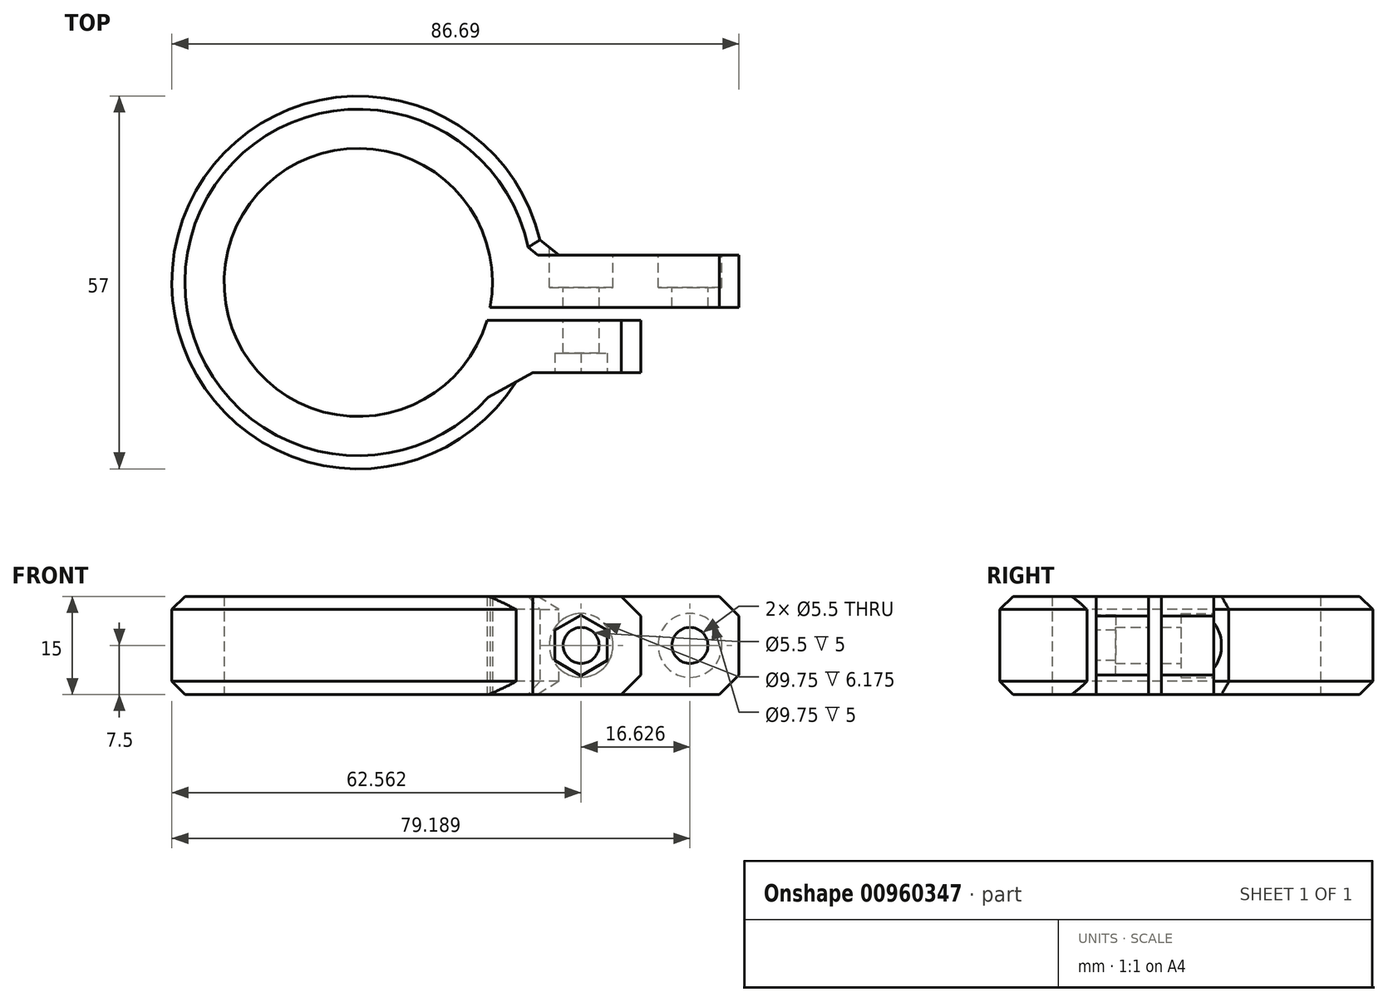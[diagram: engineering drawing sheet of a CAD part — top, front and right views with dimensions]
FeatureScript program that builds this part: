
annotation { "Feature Type Name" : "Feature", "Feature Type Description" : "" }
export const myFeature = defineFeature(function(context is Context, id is Id, definition is map)
    precondition{}
    {
        {
            var Q0;
            Q0=qCreatedBy(makeId("Top.planeOp"),FACE);
            var sketch = newSketch(context, id + "F0", { "sketchPlane" : qUnion([Q0])});
            skArc(sketch, "E0", {"start": v(20.14, -3.8) * mm, "mid": v(-19.93, 4.8) * mm, "end": v(19.66, -5.8) * mm});
            skLineSegment(sketch, "E1.bottom", {"start": v(43.19, -13.8) * mm, "end": v(24.94, -13.8) * mm});
            skLineSegment(sketch, "E1.top", {"start": v(43.19, 4.2) * mm, "end": v(28.19, 4.2) * mm});
            skLineSegment(sketch, "E1.left", {"start": v(43.19, -13.8) * mm, "end": v(43.19, -5.8) * mm});
            skLineSegment(sketch, "E2.bottom", {"start": v(43.19, -5.8) * mm, "end": v(19.66, -5.8) * mm});
            skLineSegment(sketch, "E2.top", {"start": v(43.19, -3.8) * mm, "end": v(20.14, -3.8) * mm});
            skLineSegment(sketch, "E3.trimOffspring", {"start": v(43.19, -3.8) * mm, "end": v(43.19, 4.2) * mm});
            skArc(sketch, "E4.trimOffspring", {"start": v(28.19, 4.2) * mm, "mid": v(-28.05, 5.07) * mm, "end": v(24.94, -13.8) * mm});
            skLineSegment(sketch, "E5", {"start": v(25.49, 0) * mm, "end": v(25.49, -3.8) * mm, "construction": true});
            skLineSegment(sketch, "E6", {"start": v(-37.17, 0) * mm, "end": v(70.98, 0) * mm, "construction": true});
            skSolve(sketch);
        }
        {
            var Q0;
            Q0 = qSketchRegion(id + "F0", true);
            extrude(context, id + "F1", {"entities" : qUnion([Q0]), "depth" : 15 * mm, "offsetDistance" : 25 * mm});
        }
        {
            var Q0;
            Q0=makeQuery(id+"F1.opExtrude","SWEPT_FACE",FACE,{"disambiguationData":[OSD([sQuery(id+"F0.wireOp",EDGE,"E3.trimOffspring")])]});
            extrude(context, id + "F2", {"entities" : qUnion([Q0]), "operationType" : NewBodyOperationType.ADD, "depth" : 15 * mm, "offsetDistance" : 25 * mm});
        }
        {
            var Q0;
            {var subQ0=sQuery(id+"F0.wireOp",EDGE,"E1.top");Q0=makeQuery(id+"F2.boolean.opBoolean","MERGE",FACE,{"derivedFrom":[makeQuery(id+"F1.opExtrude","SWEPT_FACE",FACE,{"disambiguationData":[OSD([subQ0])]}),makeQuery(id+"F2.opExtrude","SWEPT_FACE",FACE,{"disambiguationData":[OSD([subQ0,sQuery(id+"F0.wireOp",EDGE,"E3.trimOffspring")])]})]});}
            var sketch = newSketch(context, id + "F3", { "sketchPlane" : qUnion([Q0])});
            skLineSegment(sketch, "E7", {"start": v(-24.94, 15) * mm, "end": v(-43.19, 0) * mm, "construction": true});
            skLineSegment(sketch, "E8", {"start": v(-43.19, 15) * mm, "end": v(-24.94, 0) * mm, "construction": true});
            skPoint(sketch, "E9", {"position": v(-34.06, 7.5) * mm});
            skSolve(sketch);
        }
        {
            var Q0;
            Q0=sQuery(id+"F3.wireOp",VERTEX,"E9");
            var Q1;
            Q1=makeQuery(id+"F1.opExtrude","SWEPT_BODY",BODY,{"disambiguationData":[OSD([sQuery(id+"F0.wireOp",EDGE,"E0"),sQuery(id+"F0.wireOp",EDGE,"E1.bottom"),sQuery(id+"F0.wireOp",EDGE,"E1.top"),sQuery(id+"F0.wireOp",EDGE,"E1.left"),sQuery(id+"F0.wireOp",EDGE,"E2.bottom"),sQuery(id+"F0.wireOp",EDGE,"E2.top"),sQuery(id+"F0.wireOp",EDGE,"E3.trimOffspring"),sQuery(id+"F0.wireOp",EDGE,"E4.trimOffspring")])]});
            hole(context, id + "F4", {"style" : HoleStyle.C_BORE, "endStyle" : HoleEndStyle.BLIND, "standardTappedOrClearance" : lookupTablePath({ "fit" : "Normal", "standard" : "ISO", "size" : "M5", "type" : "Clearance" }), "standardBlindInLast" : lookupTablePath({ "fit" : "Normal", "standard" : "ISO", "engagement" : "75%", "pitch" : "0.8 mm", "size" : "M5", "type" : "Clearance & tapped" }), "holeDiameter" : 5.5 * mm, "cBoreDiameter" : 9.75 * mm, "cBoreDepth" : 5 * mm, "majorDiameter" : 5 * mm, "holeDepth" : 40 * mm, "tappedDepth" : 19.5 * mm, "tapClearance" : 3, "startFromSketch" : true, "locations" : qUnion([Q0]), "scope" : qUnion([Q1])});
        }
        {
            var Q0;
            Q0=makeQuery(id+"F1.opExtrude","CAP_EDGE",EDGE,{"disambiguationData":[OSD([sQuery(id+"F0.wireOp",EDGE,"E1.left")])],"isStart":false});
            var Q1;
            Q1=makeQuery(id+"F1.opExtrude","CAP_EDGE",EDGE,{"disambiguationData":[OSD([sQuery(id+"F0.wireOp",EDGE,"E1.left")])],"isStart":true});
            var Q2;
            Q2=makeQuery(id+"F1.opExtrude","SWEPT_EDGE",EDGE,{"disambiguationData":[OSD([sQuery(id+"F0.wireOp",EDGE,"E1.bottom"),sQuery(id+"F0.wireOp",EDGE,"E4.trimOffspring")])]});
            var Q3;
            {var subQ0=sQuery(id+"F0.wireOp",EDGE,"E3.trimOffspring");Q3=makeQuery(id+"F2.opExtrude","CAP_EDGE",EDGE,{"disambiguationData":[OSD([subQ0]),TDD([makeQuery(id+"F1.opExtrude","CAP_EDGE",EDGE,{"disambiguationData":[OSD([subQ0])],"isStart":false})])],"isStart":false});}
            var Q4;
            {var subQ0=sQuery(id+"F0.wireOp",EDGE,"E3.trimOffspring");Q4=makeQuery(id+"F2.opExtrude","CAP_EDGE",EDGE,{"disambiguationData":[OSD([subQ0]),TDD([makeQuery(id+"F1.opExtrude","CAP_EDGE",EDGE,{"disambiguationData":[OSD([subQ0])],"isStart":true})])],"isStart":false});}
            var Q5;
            Q5=makeQuery(id+"F1.opExtrude","SWEPT_EDGE",EDGE,{"disambiguationData":[OSD([sQuery(id+"F0.wireOp",EDGE,"E1.top"),sQuery(id+"F0.wireOp",EDGE,"E4.trimOffspring")])]});
            chamfer(context, id + "F5", {"entities" : qUnion([Q0, Q1, Q2, Q3, Q4, Q5]), "width" : 3 * mm, "tangentPropagation" : true});
        }
        {
            var Q0;
            {var subQ0=sQuery(id+"F0.wireOp",EDGE,"E1.top");Q0=makeQuery(id+"F2.boolean.opBoolean","MERGE",FACE,{"derivedFrom":[makeQuery(id+"F1.opExtrude","SWEPT_FACE",FACE,{"disambiguationData":[OSD([subQ0])]}),makeQuery(id+"F2.opExtrude","SWEPT_FACE",FACE,{"disambiguationData":[OSD([subQ0,sQuery(id+"F0.wireOp",EDGE,"E3.trimOffspring")])]})]});}
            var sketch = newSketch(context, id + "F6", { "sketchPlane" : qUnion([Q0])});
            skLineSegment(sketch, "E10", {"start": v(-43.19, 15) * mm, "end": v(-43.19, 0) * mm, "construction": true});
            skLineSegment(sketch, "E11", {"start": v(-43.19, 15) * mm, "end": v(-58.19, 0) * mm, "construction": true});
            skLineSegment(sketch, "E12", {"start": v(-58.19, 15) * mm, "end": v(-43.19, 0) * mm, "construction": true});
            skPoint(sketch, "E13", {"position": v(-50.69, 7.5) * mm});
            skLineSegment(sketch, "E14", {"start": v(-58.19, 0) * mm, "end": v(-58.19, 15) * mm, "construction": true});
            skSolve(sketch);
        }
        {
            var Q0;
            Q0=sQuery(id+"F6.wireOp",VERTEX,"E13");
            var Q1;
            Q1=makeQuery(id+"F1.opExtrude","SWEPT_BODY",BODY,{"disambiguationData":[OSD([sQuery(id+"F0.wireOp",EDGE,"E0"),sQuery(id+"F0.wireOp",EDGE,"E1.bottom"),sQuery(id+"F0.wireOp",EDGE,"E1.top"),sQuery(id+"F0.wireOp",EDGE,"E1.left"),sQuery(id+"F0.wireOp",EDGE,"E2.bottom"),sQuery(id+"F0.wireOp",EDGE,"E2.top"),sQuery(id+"F0.wireOp",EDGE,"E3.trimOffspring"),sQuery(id+"F0.wireOp",EDGE,"E4.trimOffspring")])]});
            hole(context, id + "F7", {"style" : HoleStyle.C_BORE, "endStyle" : HoleEndStyle.BLIND, "standardTappedOrClearance" : lookupTablePath({ "fit" : "Normal", "standard" : "ISO", "size" : "M5", "type" : "Clearance" }), "standardBlindInLast" : lookupTablePath({ "fit" : "Normal", "standard" : "ISO", "engagement" : "75%", "pitch" : "0.8 mm", "size" : "M5", "type" : "Clearance & tapped" }), "holeDiameter" : 5.5 * mm, "cBoreDiameter" : 9.75 * mm, "cBoreDepth" : 5 * mm, "majorDiameter" : 5 * mm, "holeDepth" : 40 * mm, "tappedDepth" : 19.5 * mm, "tapClearance" : 3, "startFromSketch" : true, "locations" : qUnion([Q0]), "scope" : qUnion([Q1])});
        }
        {
            var Q0;
            Q0=makeQuery(id+"F1.opExtrude","SWEPT_FACE",FACE,{"disambiguationData":[OSD([sQuery(id+"F0.wireOp",EDGE,"E1.bottom")])]});
            var sketch = newSketch(context, id + "F8", { "sketchPlane" : qUnion([Q0])});
            skCircle(sketch, "E15.cCircle", {"center": v(34.06, 7.5) * mm, "radius": 4 * mm, "construction": true});
            skLineSegment(sketch, "E15.0", {"start": v(38.06, 9.8) * mm, "end": v(38.06, 5.2) * mm});
            skLineSegment(sketch, "E15.1", {"start": v(38.06, 5.2) * mm, "end": v(34.06, 2.88) * mm});
            skLineSegment(sketch, "E15.2", {"start": v(34.06, 2.88) * mm, "end": v(30.06, 5.2) * mm});
            skLineSegment(sketch, "E15.3", {"start": v(30.06, 5.2) * mm, "end": v(30.06, 9.8) * mm});
            skLineSegment(sketch, "E15.4", {"start": v(30.06, 9.8) * mm, "end": v(34.06, 12.12) * mm});
            skLineSegment(sketch, "E15.5", {"start": v(34.06, 12.12) * mm, "end": v(38.06, 9.8) * mm});
            skPoint(sketch, "E15.0.midPoint", {"position": v(38.06, 7.5) * mm});
            skSolve(sketch);
        }
        {
            var Q0;
            Q0 = qSketchRegion(id + "F8", true);
            extrude(context, id + "F9", {"entities" : qUnion([Q0]), "operationType" : NewBodyOperationType.REMOVE, "oppositeDirection" : true, "depth" : 3 * mm, "offsetDistance" : 25 * mm, "hasSecondDirection" : true, "secondDirectionOppositeDirection" : false, "secondDirectionDepth" : 25 * mm});
        }
        {
            var Q0;
            Q0=makeQuery(id+"F1.opExtrude","CAP_EDGE",EDGE,{"disambiguationData":[OSD([sQuery(id+"F0.wireOp",EDGE,"E4.trimOffspring")])],"isStart":false});
            var Q1;
            Q1=makeQuery(id+"F1.opExtrude","CAP_EDGE",EDGE,{"disambiguationData":[OSD([sQuery(id+"F0.wireOp",EDGE,"E4.trimOffspring")])],"isStart":true});
            var Q2;
            {var subQ0=sQuery(id+"F0.wireOp",EDGE,"E3.trimOffspring");var subQ1=sQuery(id+"F0.wireOp",EDGE,"E4.trimOffspring");var subQ2=sQuery(id+"F0.wireOp",EDGE,"E1.top");Q2=makeQuery(id+"F5.opChamfer","BLEND_EDGE",EDGE,{"blendedFrom":[makeQuery(id+"F1.opExtrude","SWEPT_EDGE",EDGE,{"disambiguationData":[OSD([subQ2,subQ1])]}),makeQuery(id+"F2.boolean.opBoolean","MERGE",FACE,{"derivedFrom":[makeQuery(id+"F1.opExtrude","CAP_FACE",FACE,{"disambiguationData":[OSD([sQuery(id+"F0.wireOp",EDGE,"E0"),sQuery(id+"F0.wireOp",EDGE,"E1.bottom"),subQ2,sQuery(id+"F0.wireOp",EDGE,"E1.left"),sQuery(id+"F0.wireOp",EDGE,"E2.bottom"),sQuery(id+"F0.wireOp",EDGE,"E2.top"),subQ0,subQ1])],"isStart":false}),makeQuery(id+"F2.opExtrude","SWEPT_FACE",FACE,{"disambiguationData":[OSD([subQ0]),TDD([makeQuery(id+"F1.opExtrude","CAP_EDGE",EDGE,{"disambiguationData":[OSD([subQ0])],"isStart":false})])]})]})],"blendedInto":[makeQuery(id+"F2.boolean.opBoolean","MERGE",FACE,{"derivedFrom":[makeQuery(id+"F1.opExtrude","CAP_FACE",FACE,{"disambiguationData":[OSD([sQuery(id+"F0.wireOp",EDGE,"E0"),sQuery(id+"F0.wireOp",EDGE,"E1.bottom"),subQ2,sQuery(id+"F0.wireOp",EDGE,"E1.left"),sQuery(id+"F0.wireOp",EDGE,"E2.bottom"),sQuery(id+"F0.wireOp",EDGE,"E2.top"),subQ0,subQ1])],"isStart":false}),makeQuery(id+"F2.opExtrude","SWEPT_FACE",FACE,{"disambiguationData":[OSD([subQ0]),TDD([makeQuery(id+"F1.opExtrude","CAP_EDGE",EDGE,{"disambiguationData":[OSD([subQ0])],"isStart":false})])]})]})]});}
            var Q3;
            {var subQ0=sQuery(id+"F0.wireOp",EDGE,"E3.trimOffspring");var subQ1=sQuery(id+"F0.wireOp",EDGE,"E4.trimOffspring");var subQ2=sQuery(id+"F0.wireOp",EDGE,"E1.top");Q3=makeQuery(id+"F5.opChamfer","BLEND_EDGE",EDGE,{"blendedFrom":[makeQuery(id+"F1.opExtrude","SWEPT_EDGE",EDGE,{"disambiguationData":[OSD([subQ2,subQ1])]}),makeQuery(id+"F2.boolean.opBoolean","MERGE",FACE,{"derivedFrom":[makeQuery(id+"F1.opExtrude","CAP_FACE",FACE,{"disambiguationData":[OSD([sQuery(id+"F0.wireOp",EDGE,"E0"),sQuery(id+"F0.wireOp",EDGE,"E1.bottom"),subQ2,sQuery(id+"F0.wireOp",EDGE,"E1.left"),sQuery(id+"F0.wireOp",EDGE,"E2.bottom"),sQuery(id+"F0.wireOp",EDGE,"E2.top"),subQ0,subQ1])],"isStart":true}),makeQuery(id+"F2.opExtrude","SWEPT_FACE",FACE,{"disambiguationData":[OSD([subQ0]),TDD([makeQuery(id+"F1.opExtrude","CAP_EDGE",EDGE,{"disambiguationData":[OSD([subQ0])],"isStart":true})])]})]})],"blendedInto":[makeQuery(id+"F2.boolean.opBoolean","MERGE",FACE,{"derivedFrom":[makeQuery(id+"F1.opExtrude","CAP_FACE",FACE,{"disambiguationData":[OSD([sQuery(id+"F0.wireOp",EDGE,"E0"),sQuery(id+"F0.wireOp",EDGE,"E1.bottom"),subQ2,sQuery(id+"F0.wireOp",EDGE,"E1.left"),sQuery(id+"F0.wireOp",EDGE,"E2.bottom"),sQuery(id+"F0.wireOp",EDGE,"E2.top"),subQ0,subQ1])],"isStart":true}),makeQuery(id+"F2.opExtrude","SWEPT_FACE",FACE,{"disambiguationData":[OSD([subQ0]),TDD([makeQuery(id+"F1.opExtrude","CAP_EDGE",EDGE,{"disambiguationData":[OSD([subQ0])],"isStart":true})])]})]})]});}
            chamfer(context, id + "F10", {"entities" : qUnion([Q0, Q1, Q2, Q3]), "width" : 2 * mm, "tangentPropagation" : true});
        }
    });
